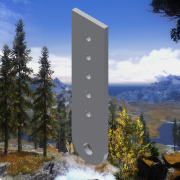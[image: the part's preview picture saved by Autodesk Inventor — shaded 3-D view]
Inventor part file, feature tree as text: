
AUTODESK INVENTOR PART (.ipt)
format: ipt  version: 2015 SP1 (Build 190203100, 203)  size: 184,832 bytes
history: native  units: in
note: dims shown in document units (in); Inventor stores cm internally (conversion verified against a paired STEP export)
features: sketch x3, extrude x2, hole x2, fillet x1, projected_geometry x1
ambient origin geometry x8: Origin, YZ Plane, XZ Plane, XY Plane, X Axis, Y Axis, Z Axis, Center Point
bodies: Solid1 (feature_tree)
feature tree (9):
  extrude  "Extrusion1"  Depth=0.5in
  sketch  "Sketch2"  dims[d2=1.0in d3=0.375in d4=2.81in]
  hole  "Hole1"  [1 undecoded]
  fillet  "Fillet2"  Radius=2.81in
  extrude  "Extrusion2"  Depth=0.5in
  hole  "Hole2"  [1 undecoded]
  sketch  "Sketch1"  dims[d0=0.281in d1=0.5in]
  sketch  "Sketch3"  dims[d5=0.125in d6=0.0in d8=0.5in d10=0.161in d11=0.75in d12=0.119in d13=0.25in d14=0.5635in d15=1.0in d16=0.8108in d18=0.5in d20=0.5in d21=1.0in d22=0.0in d23=0.161in d24=0.75in d25=0.375in d26=0.25in d27=0.5635in d28=1.0in d29=0.8108in d30=0.5in d31=1.71in]
  projected_geometry  "Projected Loop1"
note: 2 required parameter values undecoded (feature->parameter linkage not recoverable at this tier; creation-order binding heuristic only, values carry confidence <= 0.55)
